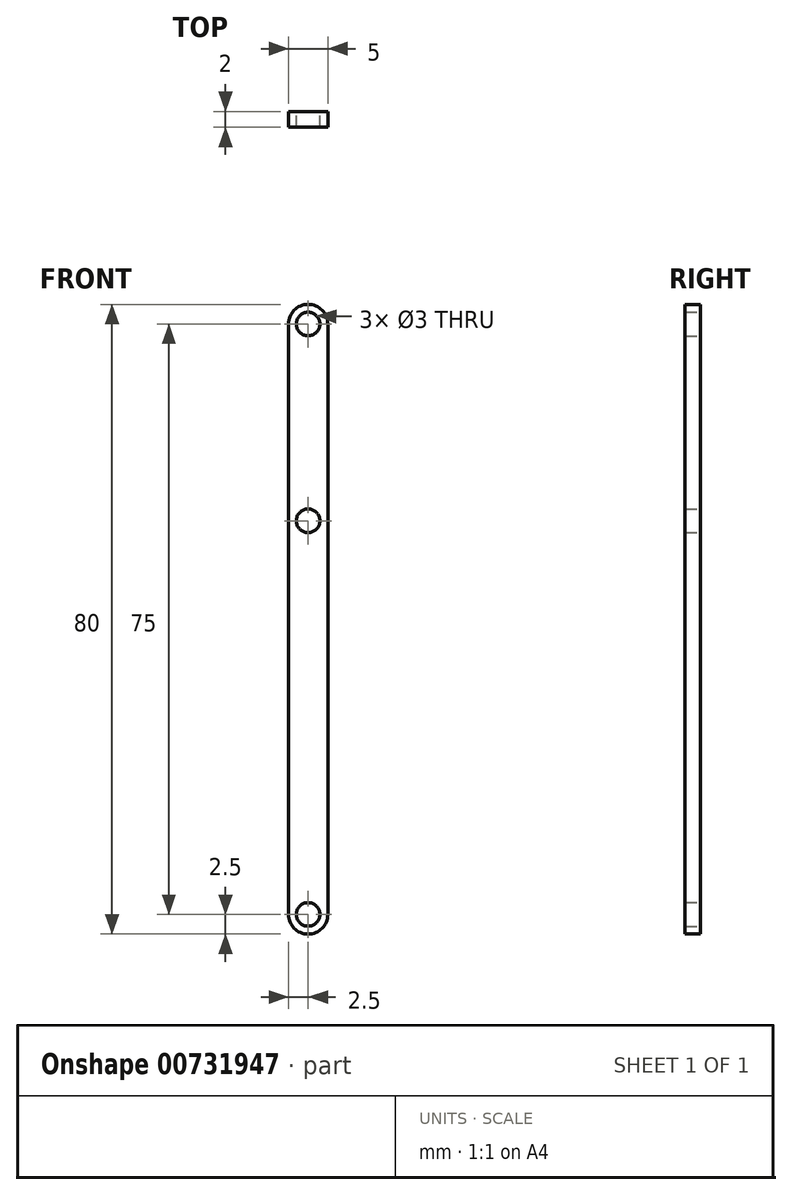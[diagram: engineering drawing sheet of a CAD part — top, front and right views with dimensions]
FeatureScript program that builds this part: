
annotation { "Feature Type Name" : "Feature", "Feature Type Description" : "" }
export const myFeature = defineFeature(function(context is Context, id is Id, definition is map)
    precondition{}
    {
        {
            var Q0;
            Q0=qCreatedBy(makeId("Front.planeOp"),FACE);
            var sketch = newSketch(context, id + "F0", { "sketchPlane" : qUnion([Q0])});
            skCircle(sketch, "E0", {"center": v(0, 37.5) * mm, "radius": 1.5 * mm});
            skCircle(sketch, "E1", {"center": v(0, -37.5) * mm, "radius": 1.5 * mm});
            skArc(sketch, "E2", {"start": v(2.5, 37.5) * mm, "mid": v(0, 40) * mm, "end": v(-2.5, 37.5) * mm});
            skArc(sketch, "E3", {"start": v(-2.5, -37.5) * mm, "mid": v(0, -40) * mm, "end": v(2.5, -37.5) * mm});
            skLineSegment(sketch, "E4", {"start": v(2.5, 37.5) * mm, "end": v(2.5, -37.5) * mm});
            skLineSegment(sketch, "E5", {"start": v(-2.5, 37.5) * mm, "end": v(-2.5, -37.5) * mm});
            skCircle(sketch, "E6", {"center": v(0, 12.5) * mm, "radius": 1.5 * mm});
            skSolve(sketch);
        }
        {
            var Q0;
            Q0 = qSketchRegion(id + "F0", true);
            extrude(context, id + "F1", {"entities" : qUnion([Q0]), "depth" : 2 * mm, "offsetDistance" : 25 * mm});
        }
    });
